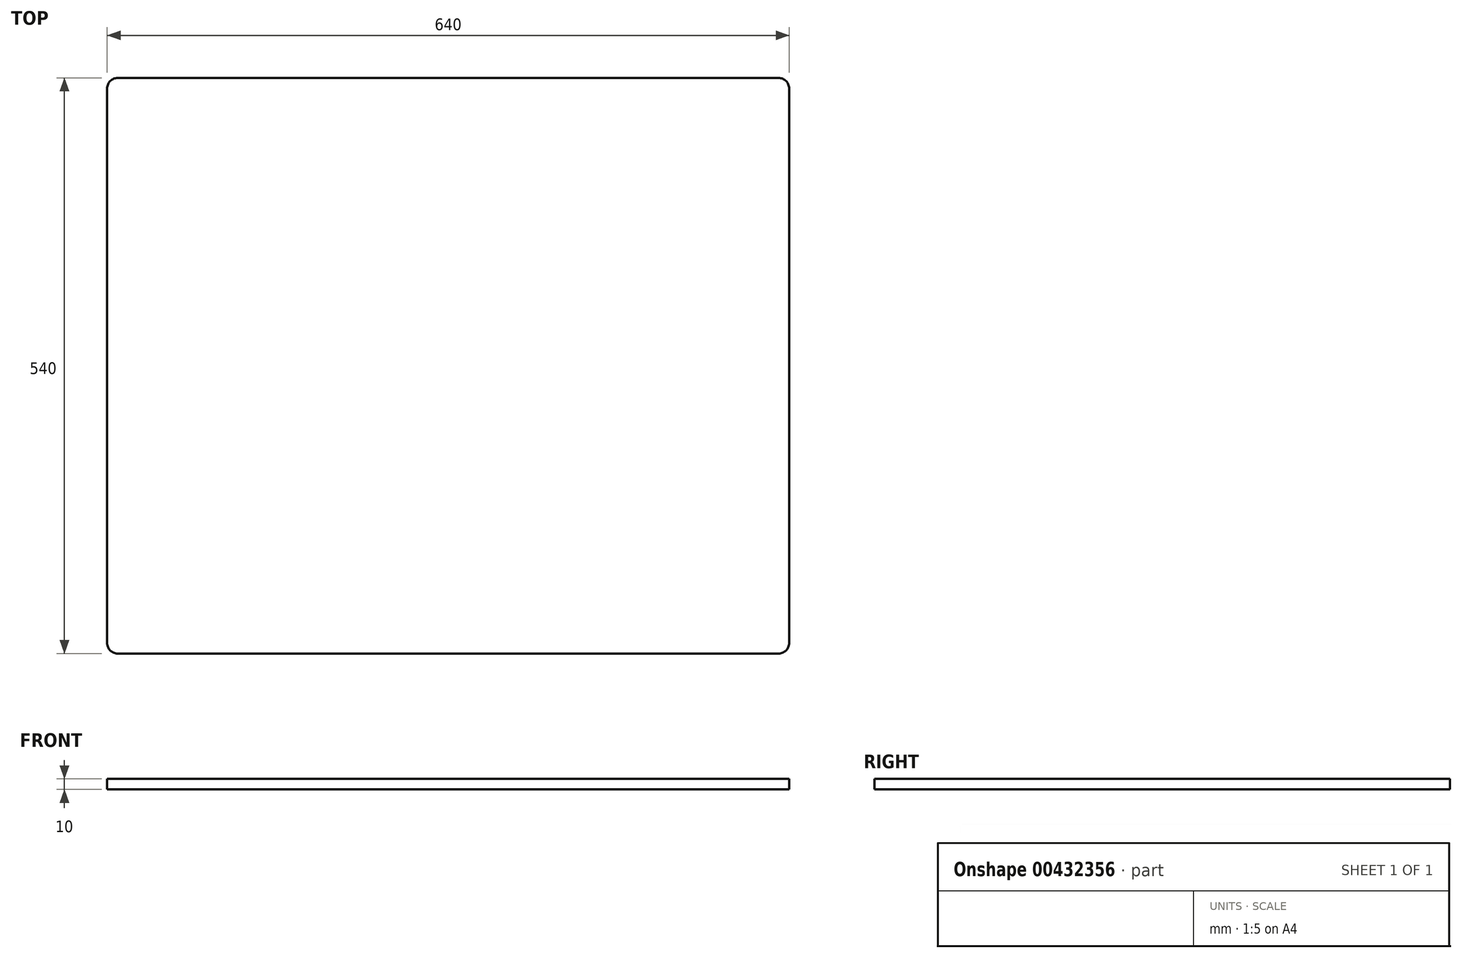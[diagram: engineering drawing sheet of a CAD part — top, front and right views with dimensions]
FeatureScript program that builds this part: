
annotation { "Feature Type Name" : "Feature", "Feature Type Description" : "" }
export const myFeature = defineFeature(function(context is Context, id is Id, definition is map)
    precondition{}
    {
        {
            var Q0;
            Q0=qCreatedBy(makeId("Top.planeOp"),FACE);
            var sketch = newSketch(context, id + "F0", { "sketchPlane" : qUnion([Q0])});
            skLineSegment(sketch, "E0.bottom", {"start": v(-310, 270) * mm, "end": v(310, 270) * mm});
            skLineSegment(sketch, "E0.top", {"start": v(-310, -270) * mm, "end": v(310, -270) * mm});
            skLineSegment(sketch, "E0.left", {"start": v(-320, 260) * mm, "end": v(-320, -260) * mm});
            skLineSegment(sketch, "E0.right", {"start": v(320, 260) * mm, "end": v(320, -260) * mm});
            skPoint(sketch, "E0.middle", {"position": v(0, 0) * mm});
            skPoint(sketch, "E1.visualSharp", {"position": v(-320, 270) * mm});
            skArc(sketch, "E1.filletArc", {"start": v(-310, 270) * mm, "mid": v(-317.07, 267.07) * mm, "end": v(-320, 260) * mm});
            skPoint(sketch, "E2.visualSharp", {"position": v(320, 270) * mm});
            skArc(sketch, "E2.filletArc", {"start": v(320, 260) * mm, "mid": v(317.07, 267.07) * mm, "end": v(310, 270) * mm});
            skPoint(sketch, "E3.visualSharp", {"position": v(320, -270) * mm});
            skArc(sketch, "E3.filletArc", {"start": v(310, -270) * mm, "mid": v(317.07, -267.07) * mm, "end": v(320, -260) * mm});
            skPoint(sketch, "E4.visualSharp", {"position": v(-320, -270) * mm});
            skArc(sketch, "E4.filletArc", {"start": v(-320, -260) * mm, "mid": v(-317.07, -267.07) * mm, "end": v(-310, -270) * mm});
            skSolve(sketch);
        }
        {
            var Q0;
            Q0 = qSketchRegion(id + "F0", true);
            extrude(context, id + "F1", {"entities" : qUnion([Q0]), "endBound" : BoundingType.SYMMETRIC, "depth" : 10 * mm});
        }
    });
